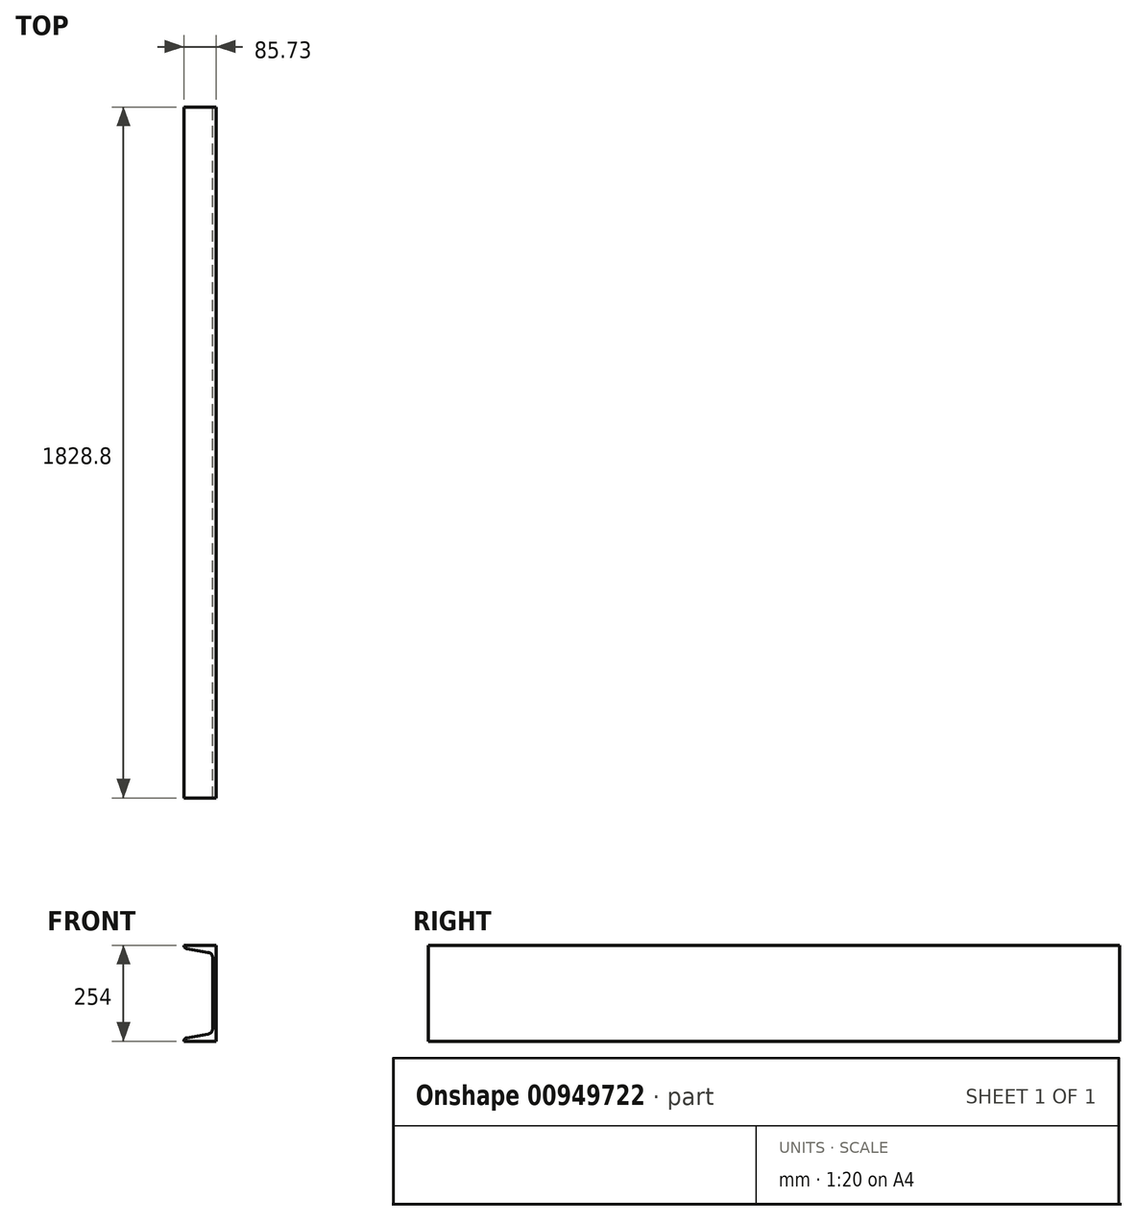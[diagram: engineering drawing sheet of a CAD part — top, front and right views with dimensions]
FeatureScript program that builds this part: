
annotation { "Feature Type Name" : "Feature", "Feature Type Description" : "" }
export const myFeature = defineFeature(function(context is Context, id is Id, definition is map)
    precondition{}
    {
        {
            var Q0;
            Q0=qCreatedBy(makeId("Front.planeOp"),FACE);
            var sketch = newSketch(context, id + "F0", { "sketchPlane" : qUnion([Q0])});
            skLineSegment(sketch, "E0", {"start": v(0, 127) * mm, "end": v(0, -127) * mm});
            skLineSegment(sketch, "E1", {"start": v(0, -127) * mm, "end": v(-85.73, -127) * mm});
            skLineSegment(sketch, "E2", {"start": v(0, 127) * mm, "end": v(-85.72, 127) * mm});
            skLineSegment(sketch, "E3", {"start": v(-9.53, 93.66) * mm, "end": v(-9.53, -93.66) * mm});
            skArc(sketch, "E4", {"start": v(-78.17, -118) * mm, "mid": v(-83.59, -121.13) * mm, "end": v(-85.73, -127) * mm});
            skArc(sketch, "E5", {"start": v(-85.73, 127) * mm, "mid": v(-83.59, 121.13) * mm, "end": v(-78.17, 118) * mm});
            skArc(sketch, "E6", {"start": v(-21.6, -108.06) * mm, "mid": v(-12.95, -103.06) * mm, "end": v(-9.53, -93.66) * mm});
            skArc(sketch, "E7", {"start": v(-9.53, 93.66) * mm, "mid": v(-12.95, 103.06) * mm, "end": v(-21.6, 108.06) * mm});
            skLineSegment(sketch, "E8", {"start": v(-78.17, -118) * mm, "end": v(-21.6, -108.06) * mm});
            skLineSegment(sketch, "E9", {"start": v(-78.17, 118) * mm, "end": v(-21.6, 108.06) * mm});
            skSolve(sketch);
        }
        {
            var Q0;
            Q0 = qSketchRegion(id + "F0", true);
            extrude(context, id + "F1", {"entities" : qUnion([Q0]), "depth" : 1828.8 * mm, "offsetDistance" : 25.4 * mm});
        }
    });
